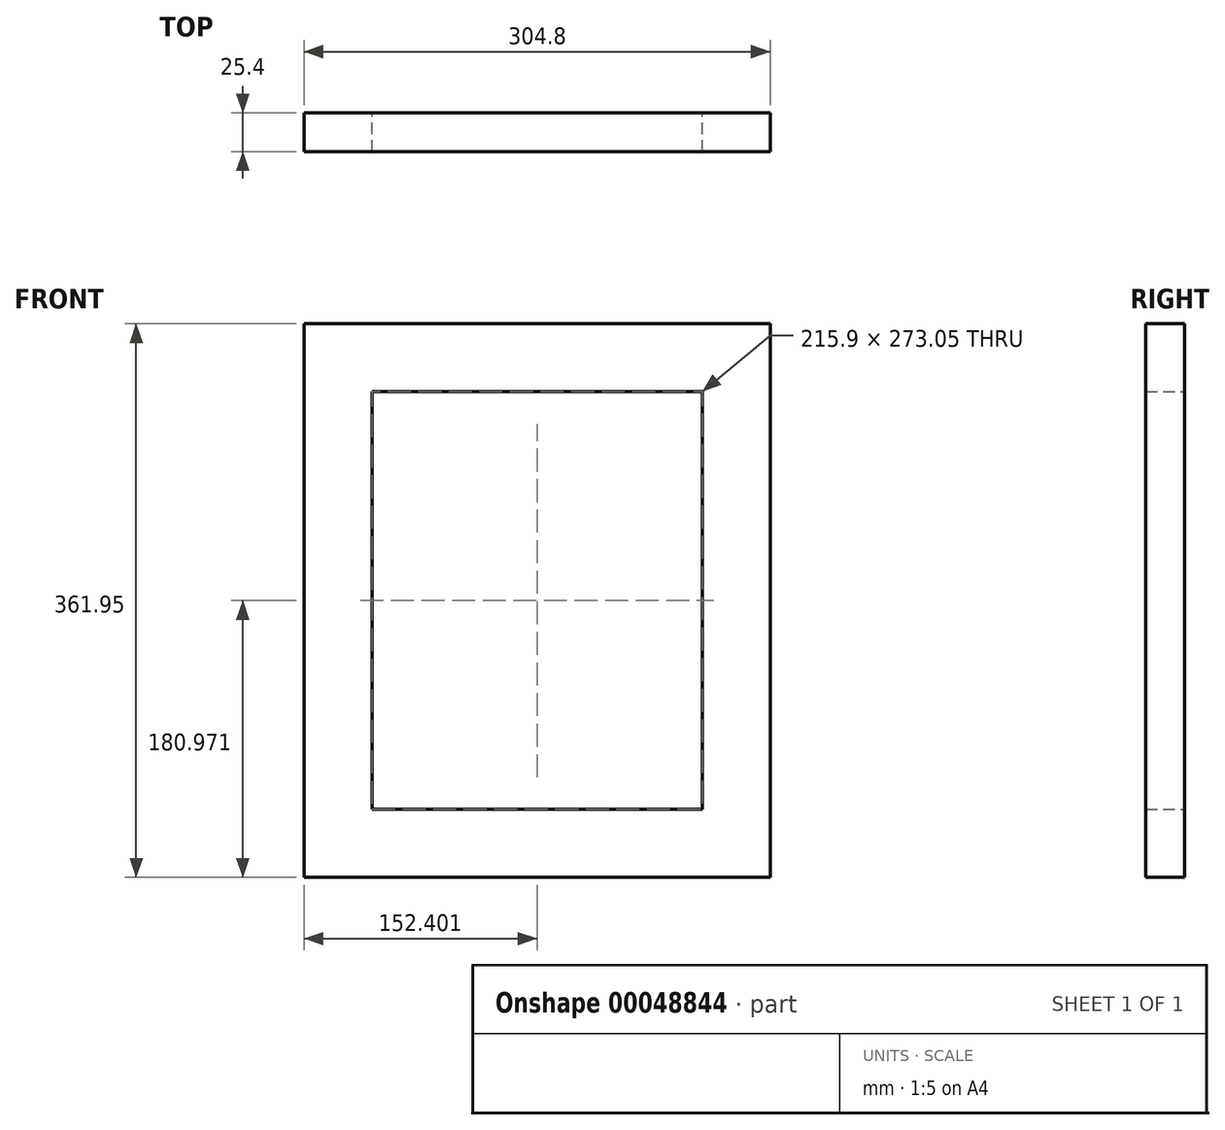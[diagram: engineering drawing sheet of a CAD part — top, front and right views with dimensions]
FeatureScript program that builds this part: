
annotation { "Feature Type Name" : "Feature", "Feature Type Description" : "" }
export const myFeature = defineFeature(function(context is Context, id is Id, definition is map)
    precondition{}
    {
        {
            var Q0;
            Q0=qCreatedBy(makeId("Front.planeOp"),FACE);
            var sketch = newSketch(context, id + "F0", { "sketchPlane" : qUnion([Q0])});
            skLineSegment(sketch, "E0.bottom", {"start": v(-165, 238.98) * mm, "end": v(139.8, 238.98) * mm});
            skLineSegment(sketch, "E0.top", {"start": v(-165, -122.97) * mm, "end": v(139.8, -122.97) * mm});
            skLineSegment(sketch, "E0.left", {"start": v(-165, 238.98) * mm, "end": v(-165, -122.97) * mm});
            skLineSegment(sketch, "E0.right", {"start": v(139.8, 238.98) * mm, "end": v(139.8, -122.97) * mm});
            skPoint(sketch, "E1", {"position": v(-120.56, 149.72) * mm});
            skPoint(sketch, "E2", {"position": v(-68.98, 194.53) * mm});
            skPoint(sketch, "E3", {"position": v(95.34, -66.36) * mm});
            skPoint(sketch, "E4", {"position": v(79.04, -78.52) * mm});
            skLineSegment(sketch, "E5.bottom", {"start": v(-120.56, 194.53) * mm, "end": v(95.34, 194.53) * mm});
            skLineSegment(sketch, "E5.top", {"start": v(-120.56, -78.52) * mm, "end": v(95.34, -78.52) * mm});
            skLineSegment(sketch, "E5.left", {"start": v(-120.56, 194.53) * mm, "end": v(-120.56, -78.52) * mm});
            skLineSegment(sketch, "E5.right", {"start": v(95.34, 194.53) * mm, "end": v(95.34, -78.52) * mm});
            skSolve(sketch);
        }
        {
            var Q0;
            Q0=makeQuery(id+"F0.imprint","IMPRINT",FACE,{"disambiguationData":[TD([[makeQuery(id+"F0.imprint","IMPRINT",EDGE,{"derivedFrom":sQuery(id+"F0.wireOp",EDGE,"E0.bottom")}),-1.0]])]});
            extrude(context, id + "F1", {"entities" : qUnion([Q0]), "depth" : 25.4 * mm});
        }
    });
